# Revit family: Vitra_Arkitekt_ShowerTray_5807L003-0578
name_source: partatom
category: Plumbing Fixtures
revit_build: Autodesk Revit 2017 (Build: 20160225_1515(x64)
units: mm (PartAtom-declared; Revit-internal decimal feet)

## family parameters
Cut with Voids When Loaded = No
Host = Face
OmniClass Number = 23.45.05.14.17
OmniClass Title = Showers
Part Type = Normal
Room Calculation Point = No
Round Connector Dimension = Use Diameter
Shared = Yes

## types (2) — shared parameters
BIMobject category = Sanitary - Shower trays
CW Connection = No
Color = White
Default Elevation = 850 mm  [stored 2.78871 ft]
Description = VitrA Arkitekt Shower Tray
Design country = Turkey
HW Connection = No
IFC Classification = Sanitary Terminal
Main Material = Ceramic
Manufacturer = Vitra
Manufacturer name = Vitra
Masterformat 2014 Code = 22 41 23
Masterformat 2014 Description = Residential Showers
MountingType = Floor Mounted
NBS Referans Code = 35-06-84
NBS Referans Description = Shower Trays
Nominal Depth = 900 mm
NominalHeight = 55 mm  [stored 0.180446 ft]
NominalWidth = 900 mm
OmniClass Code = 23-31 17 00
OmniClass Description = Showers
Product certification = https://vitraglobal.com
Product data url = https://www.vitra.com.tr
Product family = Floor Mounted Shower Tray
Product group = Arkitekt
Secondary Material = Vitra-Ceramic-White
Technical description = https://www.vitra.com.tr
UNSPSC Code = 301815
URL = https://vitraglobal.com
Uniclass 1.4 Code = L7214
Uniclass 1.4 Description = Showers
Uniclass 2.0 Code = PR-35-06-84
Uniclass 2.0 Description = Shower Trays
Uniclass 2015 Code = Pr_40_20_06_84
Uniclass 2015 Name = Shower trays
Uniformat II Code = D2010
Uniformat II Description = Plumbing Fixtures
Vent Connection = No
Warranty Period (Year) = 10 Years
Waste Connection = Yes
Weight Net (kg) = 31,300
Youtube = https://www.youtube.com
zero-valued in all types: Cost

## per-type parameters (varying)
| type | Article No. (default) | Model | Product SKU |
| ShowerTray-Vitra-ArkitektSeries_5807L003-0578 | 5807L003-0578 | 5807L003-0578 | 5807L003-0578 |
| ShowerTray-Vitra-ArkitektSeries_5807L203-0578 | 5807L203-0578 | 5807L203-0578 | 5807L203-0578 |

note: [stored X ft] marks values corroborated as IEEE doubles in the binary element streams (Revit-internal decimal feet)

## geometry (parser evidence)
native form markers: Sweep x3
no freeform markers — native parametric forms only
